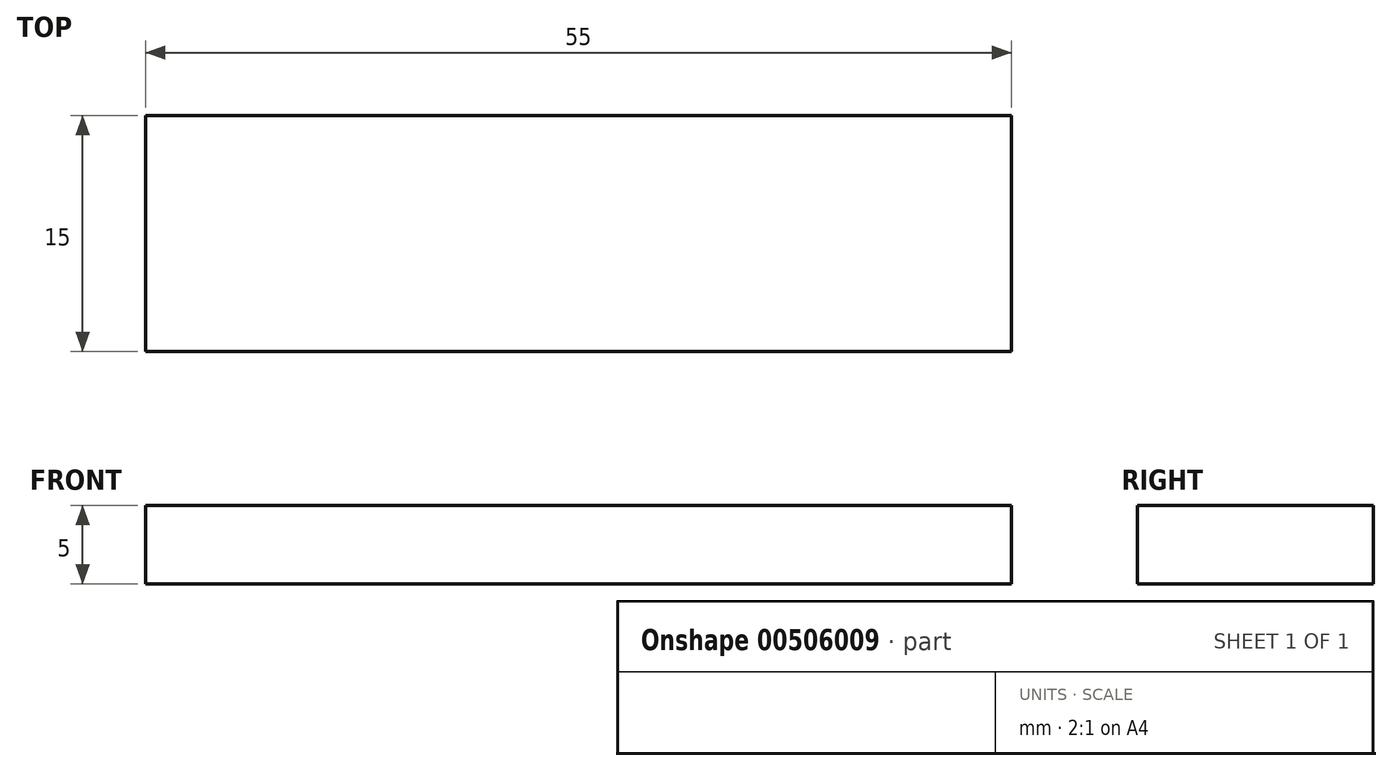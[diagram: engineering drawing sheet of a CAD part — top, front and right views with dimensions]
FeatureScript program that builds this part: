
annotation { "Feature Type Name" : "Feature", "Feature Type Description" : "" }
export const myFeature = defineFeature(function(context is Context, id is Id, definition is map)
    precondition{}
    {
        {
            var Q0;
            Q0=qCreatedBy(makeId("Top.planeOp"),FACE);
            var sketch = newSketch(context, id + "F0", { "sketchPlane" : qUnion([Q0])});
            skLineSegment(sketch, "E0.bottom", {"start": v(0, 0) * mm, "end": v(55, 0) * mm});
            skLineSegment(sketch, "E0.top", {"start": v(0, 15) * mm, "end": v(55, 15) * mm});
            skLineSegment(sketch, "E0.left", {"start": v(0, 0) * mm, "end": v(0, 15) * mm});
            skLineSegment(sketch, "E0.right", {"start": v(55, 0) * mm, "end": v(55, 15) * mm});
            skSolve(sketch);
        }
        {
            var Q0;
            Q0 = qSketchRegion(id + "F0", true);
            extrude(context, id + "F1", {"entities" : qUnion([Q0]), "depth" : 5 * mm, "offsetDistance" : 25 * mm});
        }
    });
